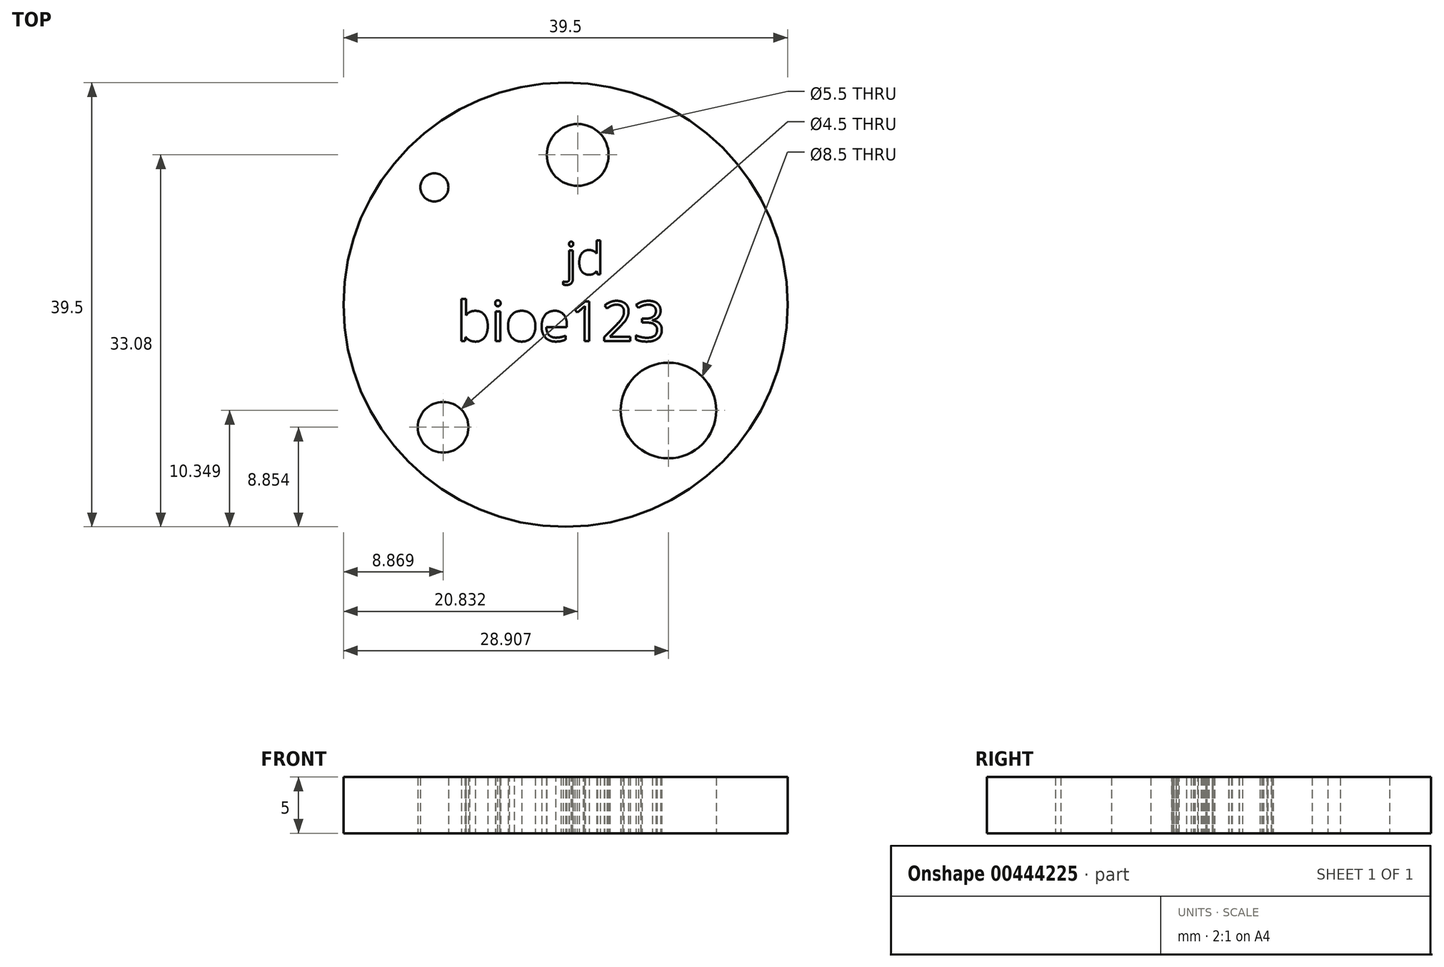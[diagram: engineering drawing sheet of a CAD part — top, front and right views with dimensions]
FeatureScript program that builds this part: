
annotation { "Feature Type Name" : "Feature", "Feature Type Description" : "" }
export const myFeature = defineFeature(function(context is Context, id is Id, definition is map)
    precondition{}
    {
        {
            var Q0;
            Q0=qCreatedBy(makeId("Top.planeOp"),FACE);
            var sketch = newSketch(context, id + "F0", { "sketchPlane" : qUnion([Q0])});
            skCircle(sketch, "E0", {"center": v(-50.55, 42.04) * mm, "radius": 495.3 * mm});
            skCircle(sketch, "E1", {"center": v(-62.21, 52.48) * mm, "radius": 1.25 * mm});
            skCircle(sketch, "E2", {"center": v(-41.4, 32.64) * mm, "radius": 4.25 * mm});
            skCircle(sketch, "E3", {"center": v(-61.43, 31.14) * mm, "radius": 2.25 * mm});
            skCircle(sketch, "E4", {"center": v(-49.47, 55.37) * mm, "radius": 2.75 * mm});
            skCircle(sketch, "E5", {"center": v(-50.55, 42.04) * mm, "radius": 19.75 * mm});
            skText(sketch, "E6", { "text": "jd", "fontName": "OpenSans-Regular.ttf"});
            skText(sketch, "E7", { "text": "bioe123", "fontName": "OpenSans-Regular.ttf"});
            const initialGuessF0  = {"E6": [-0.05055, 0.04475, 1, 0, 0.00285], "E7": [-0.06022, 0.03881, 1, 0, 0.00356]};
            skSetInitialGuess(sketch, initialGuessF0);
            skSolve(sketch);
        }
        {
            var Q0;
            Q0=makeQuery(id+"F0.imprint","IMPRINT",FACE,{"disambiguationData":[TD([[makeQuery(id+"F0.imprint","IMPRINT",EDGE,{"derivedFrom":sQuery(id+"F0.wireOp",EDGE,"E1")}),-1.0]])]});
            extrude(context, id + "F1", {"entities" : qUnion([Q0]), "depth" : 5 * mm});
        }
    });
